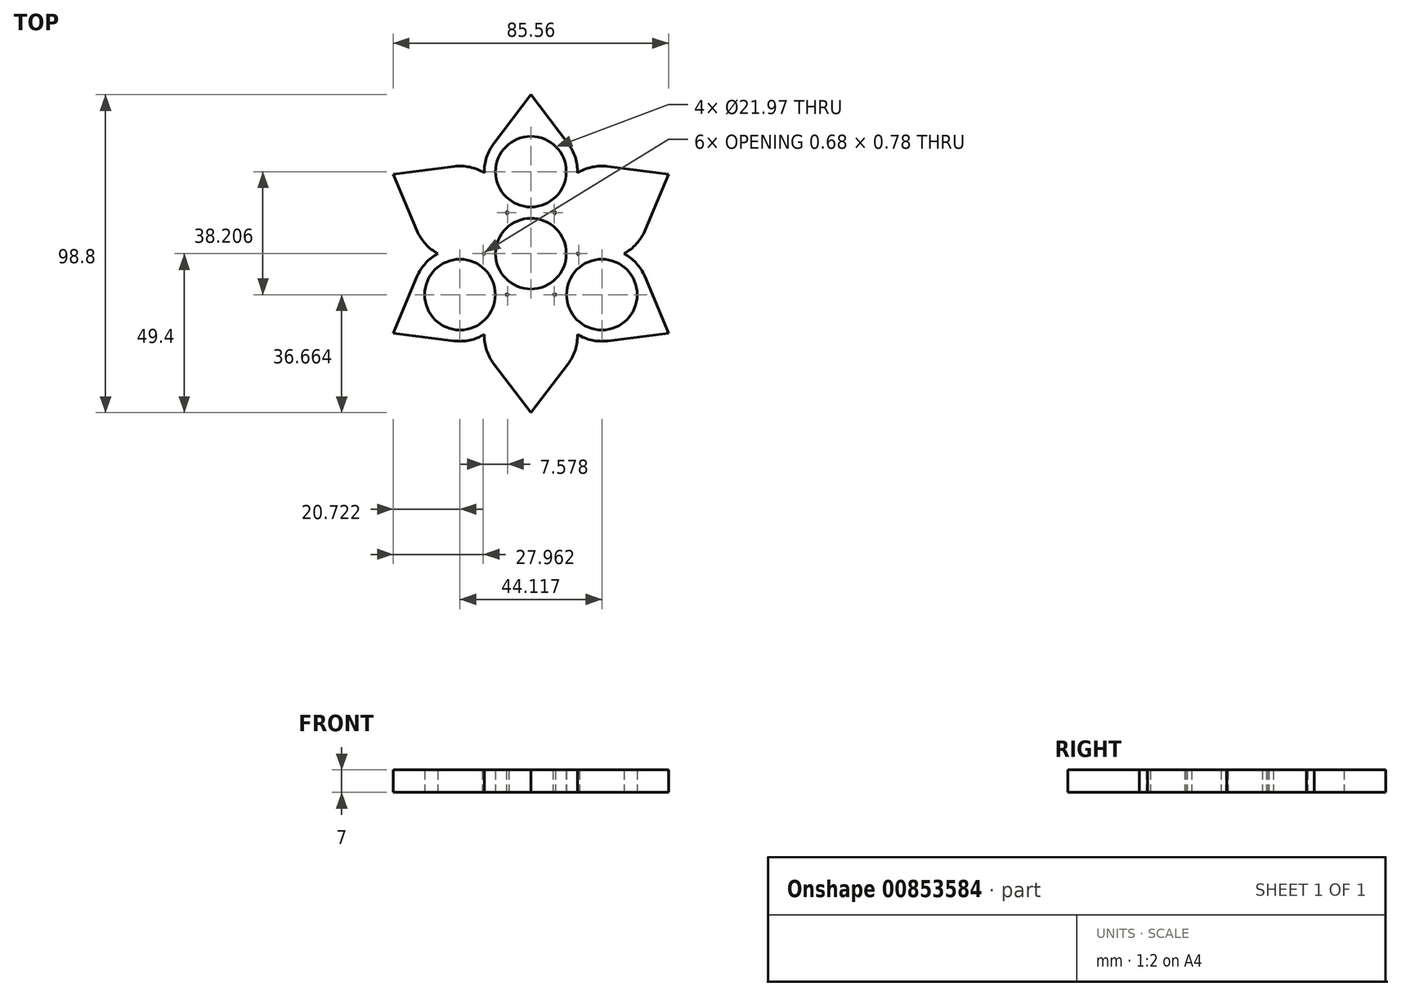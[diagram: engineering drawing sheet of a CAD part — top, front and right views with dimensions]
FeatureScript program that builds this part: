
annotation { "Feature Type Name" : "Feature", "Feature Type Description" : "" }
export const myFeature = defineFeature(function(context is Context, id is Id, definition is map)
    precondition{}
    {
        {
            var Q0;
            Q0=qCreatedBy(makeId("Top.planeOp"),FACE);
            var sketch = newSketch(context, id + "F0", { "sketchPlane" : qUnion([Q0])});
            skCircle(sketch, "E0", {"center": v(0, 0) * mm, "radius": 10.99 * mm});
            skCircle(sketch, "E1", {"center": v(0, 0) * mm, "radius": 25.47 * mm, "construction": true});
            skCircle(sketch, "E2", {"center": v(0, 25.47) * mm, "radius": 10.99 * mm});
            skCircle(sketch, "E3", {"center": v(-22.06, -12.74) * mm, "radius": 10.99 * mm});
            skCircle(sketch, "E4", {"center": v(22.06, -12.74) * mm, "radius": 10.99 * mm});
            skLineSegment(sketch, "E5", {"start": v(-22.06, -12.74) * mm, "end": v(22.06, -12.74) * mm, "construction": true});
            skLineSegment(sketch, "E6", {"start": v(0, 25.47) * mm, "end": v(-22.06, -12.74) * mm, "construction": true});
            skLineSegment(sketch, "E7", {"start": v(22.06, -12.74) * mm, "end": v(0, 25.47) * mm, "construction": true});
            skLineSegment(sketch, "E8.bottom", {"start": v(-57.15, 57.15) * mm, "end": v(57.15, 57.15) * mm, "construction": true});
            skLineSegment(sketch, "E8.top", {"start": v(-57.15, -57.15) * mm, "end": v(57.15, -57.15) * mm, "construction": true});
            skLineSegment(sketch, "E8.left", {"start": v(-57.15, 57.15) * mm, "end": v(-57.15, -57.15) * mm, "construction": true});
            skLineSegment(sketch, "E8.right", {"start": v(57.15, 57.15) * mm, "end": v(57.15, -57.15) * mm, "construction": true});
            skPoint(sketch, "E9", {"position": v(-57.15, 0) * mm});
            skPoint(sketch, "E10", {"position": v(0, 57.15) * mm});
            skSolve(sketch);
        }
        {
            var Q0;
            Q0=qCreatedBy(makeId("Top.planeOp"),FACE);
            var sketch = newSketch(context, id + "F1", { "sketchPlane" : qUnion([Q0])});
            skCircle(sketch, "E11", {"center": v(0, 0) * mm, "radius": 10.99 * mm});
            skCircle(sketch, "E12", {"center": v(-22.06, -12.74) * mm, "radius": 10.99 * mm});
            skCircle(sketch, "E13", {"center": v(0, 25.47) * mm, "radius": 10.99 * mm});
            skCircle(sketch, "E14", {"center": v(22.06, -12.74) * mm, "radius": 10.99 * mm});
            skLineSegment(sketch, "E15.bottom", {"start": v(-57.15, 57.15) * mm, "end": v(57.15, 57.15) * mm, "construction": true});
            skLineSegment(sketch, "E15.top", {"start": v(-57.15, -57.15) * mm, "end": v(57.15, -57.15) * mm, "construction": true});
            skLineSegment(sketch, "E15.left", {"start": v(-57.15, 57.15) * mm, "end": v(-57.15, -57.15) * mm, "construction": true});
            skLineSegment(sketch, "E15.right", {"start": v(57.15, 57.15) * mm, "end": v(57.15, -57.15) * mm, "construction": true});
            skPoint(sketch, "E16", {"position": v(-57.15, 0) * mm});
            skPoint(sketch, "E17", {"position": v(0, 57.15) * mm});
            skArc(sketch, "E18", {"start": v(-6.9, 12.74) * mm, "mid": v(-7.24, 12.54) * mm, "end": v(-7.58, 12.35) * mm});
            skArc(sketch, "E19", {"start": v(6.9, 12.74) * mm, "mid": v(7.24, 12.93) * mm, "end": v(7.58, 13.13) * mm});
            skArc(sketch, "E20", {"start": v(-11.53, 34.24) * mm, "mid": v(-13.79, 29.91) * mm, "end": v(-14.48, 25.08) * mm});
            skLineSegment(sketch, "E21", {"start": v(-11.53, 34.24) * mm, "end": v(0, 49.4) * mm});
            skLineSegment(sketch, "E22", {"start": v(0, 49.4) * mm, "end": v(11.53, 34.24) * mm});
            skArc(sketch, "E23.1.0", {"start": v(-35.42, 7.13) * mm, "mid": v(-32.8, 3.02) * mm, "end": v(-28.96, 0) * mm});
            skLineSegment(sketch, "E23.1.1", {"start": v(-35.42, 7.13) * mm, "end": v(-42.78, 24.7) * mm});
            skLineSegment(sketch, "E23.1.2", {"start": v(-42.78, 24.7) * mm, "end": v(-23.89, 27.1) * mm});
            skArc(sketch, "E23.1.3", {"start": v(-7.58, 12.35) * mm, "mid": v(-7.57, 12.74) * mm, "end": v(-7.58, 13.13) * mm});
            skArc(sketch, "E23.2.0", {"start": v(-23.89, -27.1) * mm, "mid": v(-19.01, -26.9) * mm, "end": v(-14.48, -25.08) * mm});
            skLineSegment(sketch, "E23.2.1", {"start": v(-23.89, -27.1) * mm, "end": v(-42.78, -24.7) * mm});
            skLineSegment(sketch, "E23.2.2", {"start": v(-42.78, -24.7) * mm, "end": v(-35.42, -7.13) * mm});
            skArc(sketch, "E23.2.3", {"start": v(-14.48, -0.4) * mm, "mid": v(-14.82, -0.2) * mm, "end": v(-15.16, 0) * mm});
            skArc(sketch, "E23.3.0", {"start": v(11.53, -34.24) * mm, "mid": v(13.79, -29.91) * mm, "end": v(14.48, -25.08) * mm});
            skLineSegment(sketch, "E23.3.1", {"start": v(11.53, -34.24) * mm, "end": v(0, -49.4) * mm});
            skLineSegment(sketch, "E23.3.2", {"start": v(0, -49.4) * mm, "end": v(-11.53, -34.24) * mm});
            skArc(sketch, "E23.3.3", {"start": v(-6.9, -12.74) * mm, "mid": v(-7.24, -12.93) * mm, "end": v(-7.58, -13.13) * mm});
            skArc(sketch, "E23.4.0", {"start": v(35.42, -7.13) * mm, "mid": v(32.8, -3.02) * mm, "end": v(28.96, 0) * mm});
            skLineSegment(sketch, "E23.4.1", {"start": v(35.42, -7.13) * mm, "end": v(42.78, -24.7) * mm});
            skLineSegment(sketch, "E23.4.2", {"start": v(42.78, -24.7) * mm, "end": v(23.89, -27.1) * mm});
            skArc(sketch, "E23.4.3", {"start": v(7.58, -12.35) * mm, "mid": v(7.57, -12.74) * mm, "end": v(7.58, -13.13) * mm});
            skArc(sketch, "E23.5.0", {"start": v(23.89, 27.1) * mm, "mid": v(19.01, 26.9) * mm, "end": v(14.48, 25.08) * mm});
            skLineSegment(sketch, "E23.5.1", {"start": v(23.89, 27.1) * mm, "end": v(42.78, 24.7) * mm});
            skLineSegment(sketch, "E23.5.2", {"start": v(42.78, 24.7) * mm, "end": v(35.42, 7.13) * mm});
            skArc(sketch, "E23.5.3", {"start": v(14.48, 0.4) * mm, "mid": v(14.82, 0.2) * mm, "end": v(15.16, 0) * mm});
            skArc(sketch, "E24.trimOffspring", {"start": v(-14.48, 25.08) * mm, "mid": v(-19.01, 26.9) * mm, "end": v(-23.89, 27.1) * mm});
            skArc(sketch, "E25.trimOffspring", {"start": v(-7.58, 13.13) * mm, "mid": v(-7.24, 12.93) * mm, "end": v(-6.9, 12.74) * mm});
            skArc(sketch, "E26.trimOffspring", {"start": v(7.58, 13.13) * mm, "mid": v(7.57, 12.74) * mm, "end": v(7.58, 12.35) * mm});
            skArc(sketch, "E27.trimOffspring", {"start": v(14.48, 25.08) * mm, "mid": v(13.79, 29.91) * mm, "end": v(11.53, 34.24) * mm});
            skArc(sketch, "E28.trimOffspring", {"start": v(7.58, 12.35) * mm, "mid": v(7.24, 12.54) * mm, "end": v(6.9, 12.74) * mm});
            skArc(sketch, "E29.trimOffspring", {"start": v(-14.48, 0.4) * mm, "mid": v(-14.49, 0) * mm, "end": v(-14.48, -0.4) * mm});
            skArc(sketch, "E30.trimOffspring", {"start": v(-28.96, 0) * mm, "mid": v(-32.8, -3.02) * mm, "end": v(-35.42, -7.13) * mm});
            skArc(sketch, "E31.trimOffspring", {"start": v(-15.16, 0) * mm, "mid": v(-14.82, 0.2) * mm, "end": v(-14.48, 0.4) * mm});
            skArc(sketch, "E32.trimOffspring", {"start": v(-14.48, -25.08) * mm, "mid": v(-13.79, -29.91) * mm, "end": v(-11.53, -34.24) * mm});
            skArc(sketch, "E33.trimOffspring", {"start": v(-7.58, -13.13) * mm, "mid": v(-7.57, -12.74) * mm, "end": v(-7.58, -12.35) * mm});
            skArc(sketch, "E34.trimOffspring", {"start": v(14.48, -0.4) * mm, "mid": v(14.49, 0) * mm, "end": v(14.48, 0.4) * mm});
            skArc(sketch, "E35.trimOffspring", {"start": v(6.9, -12.74) * mm, "mid": v(7.24, -12.54) * mm, "end": v(7.58, -12.35) * mm});
            skArc(sketch, "E36.trimOffspring", {"start": v(-7.58, -12.35) * mm, "mid": v(-7.24, -12.54) * mm, "end": v(-6.9, -12.74) * mm});
            skArc(sketch, "E37.trimOffspring", {"start": v(15.16, 0) * mm, "mid": v(14.82, -0.2) * mm, "end": v(14.48, -0.4) * mm});
            skArc(sketch, "E38.trimOffspring", {"start": v(28.96, 0) * mm, "mid": v(32.8, 3.02) * mm, "end": v(35.42, 7.13) * mm});
            skArc(sketch, "E39.trimOffspring", {"start": v(7.58, -13.13) * mm, "mid": v(7.24, -12.93) * mm, "end": v(6.9, -12.74) * mm});
            skArc(sketch, "E40.trimOffspring", {"start": v(14.48, -25.08) * mm, "mid": v(19.01, -26.9) * mm, "end": v(23.89, -27.1) * mm});
            skSolve(sketch);
        }
        {
            var Q0;
            Q0 = qSketchRegion(id + "F1", true);
            extrude(context, id + "F2", {"entities" : qUnion([Q0]), "depth" : 7 * mm, "offsetDistance" : 25.4 * mm});
        }
    });
